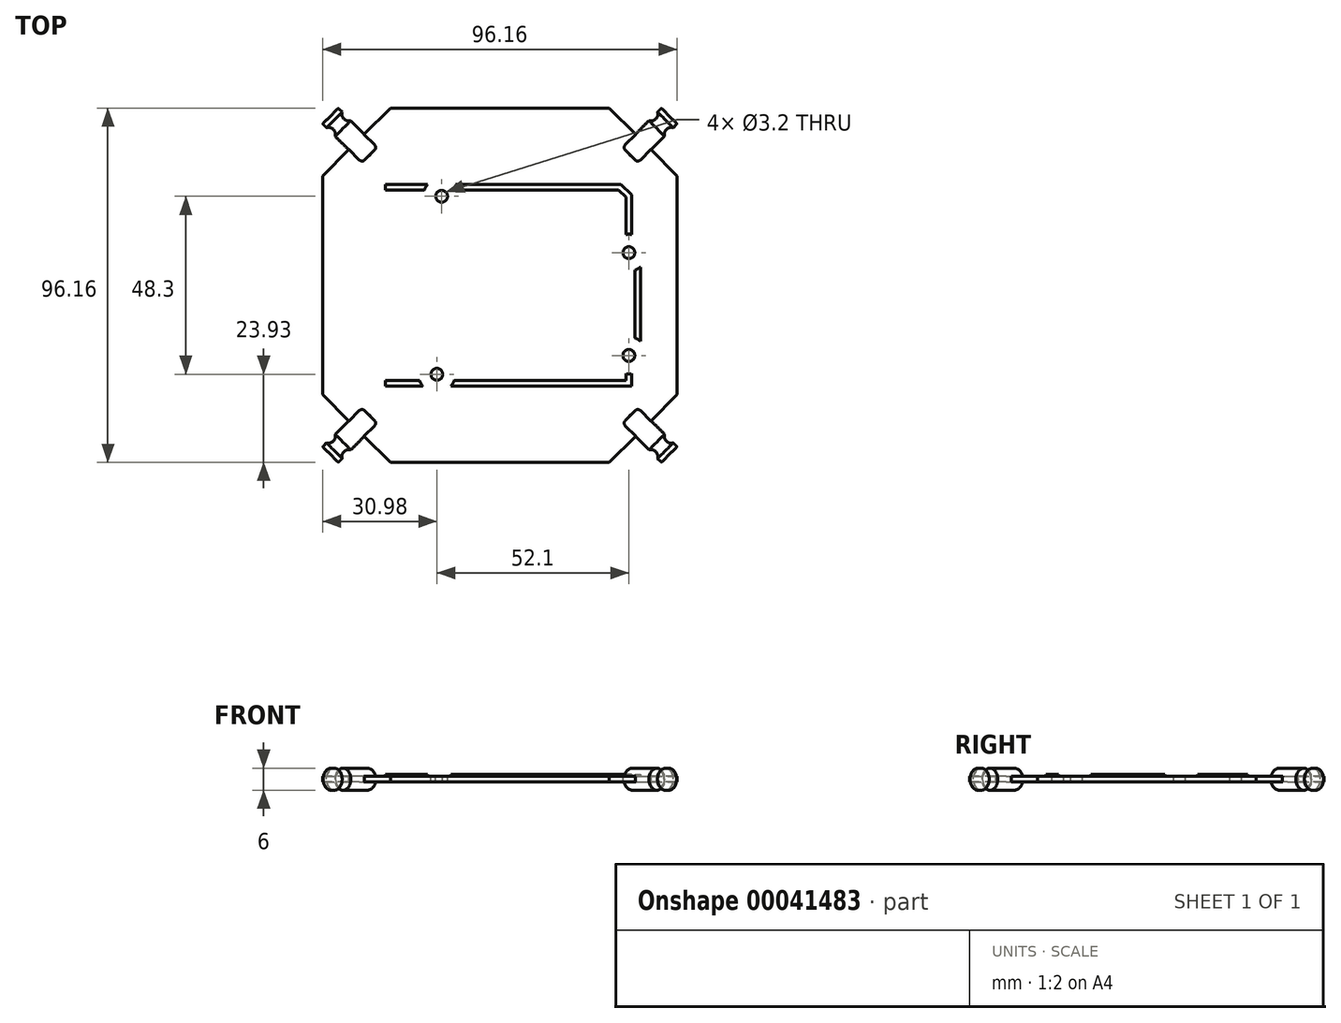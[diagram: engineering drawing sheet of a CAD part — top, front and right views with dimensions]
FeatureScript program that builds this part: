
annotation { "Feature Type Name" : "Feature", "Feature Type Description" : "" }
export const myFeature = defineFeature(function(context is Context, id is Id, definition is map)
    precondition{}
    {
        {
            var Q0;
            Q0=qCreatedBy(makeId("Top.planeOp"),FACE);
            var sketch = newSketch(context, id + "F0", { "sketchPlane" : qUnion([Q0])});
            skLineSegment(sketch, "E0", {"start": v(-43.84, 48.08) * mm, "end": v(43.84, 48.08) * mm, "construction": true});
            skLineSegment(sketch, "E1", {"start": v(48.08, 43.84) * mm, "end": v(43.84, 48.08) * mm, "construction": true});
            skLineSegment(sketch, "E2", {"start": v(48.08, 43.84) * mm, "end": v(48.08, -43.84) * mm, "construction": true});
            skLineSegment(sketch, "E3", {"start": v(48.08, -43.84) * mm, "end": v(43.84, -48.08) * mm, "construction": true});
            skLineSegment(sketch, "E4", {"start": v(43.84, -48.08) * mm, "end": v(-43.84, -48.08) * mm, "construction": true});
            skLineSegment(sketch, "E5", {"start": v(-43.84, -48.08) * mm, "end": v(-48.08, -43.84) * mm, "construction": true});
            skLineSegment(sketch, "E6", {"start": v(-48.08, -43.84) * mm, "end": v(-48.08, 43.84) * mm, "construction": true});
            skLineSegment(sketch, "E7", {"start": v(-43.84, 48.08) * mm, "end": v(-48.08, 43.84) * mm, "construction": true});
            skLineSegment(sketch, "E8", {"start": v(0, 48.08) * mm, "end": v(0, -48.08) * mm, "construction": true});
            skLineSegment(sketch, "E9", {"start": v(-48.08, 0) * mm, "end": v(48.08, 0) * mm, "construction": true});
            skSolve(sketch);
        }
        {
            var Q0;
            Q0=sQuery(id+"F0.wireOp",EDGE,"E3");
            cPlane(context, id + "F1", {"entities" : qUnion([Q0]), "cplaneType" : CPlaneType.LINE_ANGLE, "offset" : 150 * mm, "angle" : 90 * degree, "width" : 150 * mm, "height" : 150 * mm});
        }
        {
            var Q0;
            Q0=qCreatedBy(id+"F1.planeOp",FACE);
            var sketch = newSketch(context, id + "F2", { "sketchPlane" : qUnion([Q0])});
            skCircle(sketch, "E10", {"center": v(0, 0) * mm, "radius": 3 * mm});
            skSolve(sketch);
        }
        {
            var Q0;
            Q0 = qSketchRegion(id + "F2", true);
            extrude(context, id + "F3", {"entities" : qUnion([Q0]), "oppositeDirection" : true, "depth" : 15 * mm});
        }
        {
            var Q0;
            Q0=qCreatedBy(makeId("Top.planeOp"),FACE);
            var sketch = newSketch(context, id + "F4", { "sketchPlane" : qUnion([Q0])});
            skLineSegment(sketch, "E11", {"start": v(47.02, -42.78) * mm, "end": v(44.69, -40.45) * mm});
            skArc(sketch, "E12", {"start": v(44.69, -40.45) * mm, "mid": v(45.15, -42.32) * mm, "end": v(47.02, -42.78) * mm});
            skLineSegment(sketch, "E13", {"start": v(37.48, -33.23) * mm, "end": v(48.08, -43.84) * mm, "construction": true});
            skLineSegment(sketch, "E14", {"start": v(35.36, -35.36) * mm, "end": v(45.96, -45.96) * mm, "construction": true});
            skSolve(sketch);
        }
        {
            var Q0;
            Q0 = qSketchRegion(id + "F4", true);
            var Q1;
            Q1=sQuery(id+"F4.wireOp",EDGE,"E14");
            revolve(context, id + "F5", {"operationType" : NewBodyOperationType.REMOVE, "entities" : qUnion([Q0]), "axis" : qUnion([Q1]), "revolveType" : RevolveType.FULL, "oppositeDirection" : true});
        }
        {
            var Q0;
            Q0=makeQuery(id+"F3.opExtrude","CAP_EDGE",EDGE,{"disambiguationData":[OSD([sQuery(id+"F2.wireOp",EDGE,"E10")])],"isStart":true});
            fillet(context, id + "F6", {"entities" : qUnion([Q0]), "radius" : 0.3 * mm, "tangentPropagation" : true, "allowEdgeOverflow" : false});
        }
        {
            var Q0;
            Q0=makeQuery(id+"F3.opExtrude","CAP_EDGE",EDGE,{"disambiguationData":[OSD([sQuery(id+"F2.wireOp",EDGE,"E10")])],"isStart":false});
            fillet(context, id + "F7", {"entities" : qUnion([Q0]), "radius" : 1 * mm, "tangentPropagation" : true, "allowEdgeOverflow" : false});
        }
        {
            var Q0;
            Q0=qCreatedBy(makeId("Front.planeOp"),FACE);
            var sketch = newSketch(context, id + "F8", { "sketchPlane" : qUnion([Q0])});
            skLineSegment(sketch, "E15", {"start": v(0, 12.87) * mm, "end": v(0, -12.87) * mm, "construction": true});
            skSolve(sketch);
        }
        {
            var Q0;
            Q0=makeQuery(id+"F3.opExtrude","SWEPT_BODY",BODY,{"disambiguationData":[OSD([sQuery(id+"F2.wireOp",EDGE,"E10")])]});
            var Q1;
            Q1=sQuery(id+"F8.wireOp",EDGE,"E15");
            circularPattern(context, id + "F9", {"entities" : qUnion([Q0]), "axis" : qUnion([Q1]), "angle" : 90 * degree, "instanceCount" : 4});
        }
        {
            var Q0;
            Q0=qCreatedBy(makeId("Top.planeOp"),FACE);
            var sketch = newSketch(context, id + "F10", { "sketchPlane" : qUnion([Q0])});
            skLineSegment(sketch, "E16", {"start": v(-29.7, 48.08) * mm, "end": v(-48.08, 29.7) * mm});
            skLineSegment(sketch, "E17", {"start": v(-48.08, 29.7) * mm, "end": v(-48.08, -29.7) * mm});
            skLineSegment(sketch, "E18", {"start": v(-48.08, -29.7) * mm, "end": v(-29.7, -48.08) * mm});
            skLineSegment(sketch, "E19", {"start": v(-29.7, -48.08) * mm, "end": v(29.7, -48.08) * mm});
            skLineSegment(sketch, "E20", {"start": v(29.7, -48.08) * mm, "end": v(48.08, -29.7) * mm});
            skLineSegment(sketch, "E21", {"start": v(48.08, -29.7) * mm, "end": v(48.08, 29.7) * mm});
            skLineSegment(sketch, "E22", {"start": v(48.08, 29.7) * mm, "end": v(29.7, 48.08) * mm});
            skLineSegment(sketch, "E23", {"start": v(29.7, 48.08) * mm, "end": v(-29.7, 48.08) * mm});
            skSolve(sketch);
        }
        {
            var Q0;
            Q0=makeQuery(id+"F10.imprint","IMPRINT",FACE,{"disambiguationData":[TD([[makeQuery(id+"F10.imprint","IMPRINT",EDGE,{"derivedFrom":sQuery(id+"F10.wireOp",EDGE,"E16")}),1.0]])]});
            extrude(context, id + "F11", {"entities" : qUnion([Q0]), "operationType" : NewBodyOperationType.ADD, "endBound" : BoundingType.SYMMETRIC, "depth" : 1.5 * mm});
        }
        {
            var Q0;
            Q0=makeQuery(id+"F11.opExtrude","CAP_FACE",FACE,{"disambiguationData":[OSD([sQuery(id+"F10.wireOp",EDGE,"E16"),sQuery(id+"F10.wireOp",EDGE,"E17"),sQuery(id+"F10.wireOp",EDGE,"E18"),sQuery(id+"F10.wireOp",EDGE,"E19"),sQuery(id+"F10.wireOp",EDGE,"E20"),sQuery(id+"F10.wireOp",EDGE,"E21"),sQuery(id+"F10.wireOp",EDGE,"E22"),sQuery(id+"F10.wireOp",EDGE,"E23")])],"isStart":false});
            var sketch = newSketch(context, id + "F12", { "sketchPlane" : qUnion([Q0])});
            skLineSegment(sketch, "E24.bottom", {"start": v(-31.1, 26.65) * mm, "end": v(37.5, 26.65) * mm, "construction": true});
            skLineSegment(sketch, "E24.top", {"start": v(-31.1, -26.65) * mm, "end": v(37.5, -26.65) * mm, "construction": true});
            skLineSegment(sketch, "E24.left", {"start": v(-31.1, 26.65) * mm, "end": v(-31.1, -26.65) * mm, "construction": true});
            skLineSegment(sketch, "E24.right", {"start": v(37.5, 26.65) * mm, "end": v(37.5, -26.65) * mm, "construction": true});
            skCircle(sketch, "E25", {"center": v(-17.1, -24.15) * mm, "radius": 1.6 * mm});
            skCircle(sketch, "E26", {"center": v(35, -19.05) * mm, "radius": 1.6 * mm});
            skCircle(sketch, "E27", {"center": v(35, 8.85) * mm, "radius": 1.6 * mm});
            skCircle(sketch, "E28", {"center": v(-15.8, 24.15) * mm, "radius": 1.6 * mm});
            skSolve(sketch);
        }
        {
            var Q0;
            Q0=makeQuery(id+"F12.imprint","IMPRINT",FACE,{"disambiguationData":[TD([[makeQuery(id+"F12.imprint","IMPRINT",EDGE,{"derivedFrom":sQuery(id+"F12.wireOp",EDGE,"E28")}),1.0]])]});
            var Q1;
            Q1=makeQuery(id+"F12.imprint","IMPRINT",FACE,{"disambiguationData":[TD([[makeQuery(id+"F12.imprint","IMPRINT",EDGE,{"derivedFrom":sQuery(id+"F12.wireOp",EDGE,"E27")}),1.0]])]});
            var Q2;
            Q2=makeQuery(id+"F12.imprint","IMPRINT",FACE,{"disambiguationData":[TD([[makeQuery(id+"F12.imprint","IMPRINT",EDGE,{"derivedFrom":sQuery(id+"F12.wireOp",EDGE,"E25")}),1.0]])]});
            var Q3;
            Q3=makeQuery(id+"F12.imprint","IMPRINT",FACE,{"disambiguationData":[TD([[makeQuery(id+"F12.imprint","IMPRINT",EDGE,{"derivedFrom":sQuery(id+"F12.wireOp",EDGE,"E26")}),1.0]])]});
            var Q4;
            Q4=makeQuery(id+"F11.opExtrude","CAP_FACE",FACE,{"disambiguationData":[OSD([sQuery(id+"F10.wireOp",EDGE,"E16"),sQuery(id+"F10.wireOp",EDGE,"E17"),sQuery(id+"F10.wireOp",EDGE,"E18"),sQuery(id+"F10.wireOp",EDGE,"E19"),sQuery(id+"F10.wireOp",EDGE,"E20"),sQuery(id+"F10.wireOp",EDGE,"E21"),sQuery(id+"F10.wireOp",EDGE,"E22"),sQuery(id+"F10.wireOp",EDGE,"E23")])],"isStart":true});
            extrude(context, id + "F13", {"entities" : qUnion([Q0, Q1, Q2, Q3]), "operationType" : NewBodyOperationType.REMOVE, "endBound" : BoundingType.UP_TO_SURFACE, "oppositeDirection" : true, "endBoundEntityFace" : qUnion([Q4]), "depth" : 25 * mm});
        }
        {
            var Q0;
            Q0=makeQuery(id+"F12.imprint","IMPRINT",FACE,{"disambiguationData":[TD([[makeQuery(id+"F12.imprint","IMPRINT",EDGE,{"derivedFrom":sQuery(id+"F12.wireOp",EDGE,"E25")}),-1.0]])]});
            var sketch = newSketch(context, id + "F14", { "sketchPlane" : qUnion([Q0])});
            skLineSegment(sketch, "E29", {"start": v(-31.1, 27.4) * mm, "end": v(32.87, 27.4) * mm});
            skLineSegment(sketch, "E30", {"start": v(32.87, 27.4) * mm, "end": v(35.75, 24.52) * mm});
            skLineSegment(sketch, "E31", {"start": v(35.75, 24.52) * mm, "end": v(35.75, 12.48) * mm});
            skLineSegment(sketch, "E32", {"start": v(35.75, 12.48) * mm, "end": v(38.1, 10.13) * mm});
            skLineSegment(sketch, "E33", {"start": v(38.1, 10.13) * mm, "end": v(38.1, -20.33) * mm});
            skLineSegment(sketch, "E34", {"start": v(38.1, -20.33) * mm, "end": v(35.75, -22.68) * mm});
            skLineSegment(sketch, "E35", {"start": v(35.75, -22.68) * mm, "end": v(35.75, -27.4) * mm});
            skLineSegment(sketch, "E36", {"start": v(35.75, -27.4) * mm, "end": v(-31.1, -27.4) * mm});
            skLineSegment(sketch, "E37", {"start": v(-31.1, -27.4) * mm, "end": v(-31.1, -25.9) * mm});
            skLineSegment(sketch, "E38", {"start": v(-31.1, -25.9) * mm, "end": v(34.25, -25.9) * mm});
            skLineSegment(sketch, "E39", {"start": v(34.25, -25.9) * mm, "end": v(34.25, -22.06) * mm});
            skLineSegment(sketch, "E40", {"start": v(34.25, -22.06) * mm, "end": v(36.6, -19.71) * mm});
            skLineSegment(sketch, "E41", {"start": v(36.6, -19.71) * mm, "end": v(36.6, 9.51) * mm});
            skLineSegment(sketch, "E42", {"start": v(36.6, 9.51) * mm, "end": v(34.25, 11.86) * mm});
            skLineSegment(sketch, "E43", {"start": v(34.25, 11.86) * mm, "end": v(34.25, 23.9) * mm});
            skLineSegment(sketch, "E44", {"start": v(34.25, 23.9) * mm, "end": v(32.25, 25.9) * mm});
            skLineSegment(sketch, "E45", {"start": v(32.25, 25.9) * mm, "end": v(-31.1, 25.9) * mm});
            skLineSegment(sketch, "E46", {"start": v(-31.1, 25.9) * mm, "end": v(-31.1, 27.4) * mm});
            skSolve(sketch);
        }
        {
            var Q0;
            Q0 = qSketchRegion(id + "F14", true);
            extrude(context, id + "F15", {"entities" : qUnion([Q0]), "operationType" : NewBodyOperationType.ADD, "depth" : 0.5 * mm});
        }
        {
            var Q0;
            Q0=makeQuery(id+"F12.imprint","IMPRINT",FACE,{"disambiguationData":[TD([[makeQuery(id+"F12.imprint","IMPRINT",EDGE,{"derivedFrom":sQuery(id+"F12.wireOp",EDGE,"E25")}),-1.0]])]});
            var sketch = newSketch(context, id + "F16", { "sketchPlane" : qUnion([Q0])});
            skCircle(sketch, "E47", {"center": v(-15.8, 24.15) * mm, "radius": 5 * mm});
            skCircle(sketch, "E48", {"center": v(35, 8.85) * mm, "radius": 5 * mm});
            skCircle(sketch, "E49", {"center": v(35, -19.05) * mm, "radius": 5 * mm});
            skCircle(sketch, "E50", {"center": v(-17.1, -24.15) * mm, "radius": 5 * mm});
            skSolve(sketch);
        }
        {
            var Q0;
            Q0 = qSketchRegion(id + "F16", true);
            var Q1;
            Q1=makeQuery(id+"F15.opExtrude","CAP_FACE",FACE,{"disambiguationData":[OSD([sQuery(id+"F14.wireOp",EDGE,"E29"),sQuery(id+"F14.wireOp",EDGE,"E30"),sQuery(id+"F14.wireOp",EDGE,"E31"),sQuery(id+"F14.wireOp",EDGE,"E32"),sQuery(id+"F14.wireOp",EDGE,"E33"),sQuery(id+"F14.wireOp",EDGE,"E34"),sQuery(id+"F14.wireOp",EDGE,"E35"),sQuery(id+"F14.wireOp",EDGE,"E36"),sQuery(id+"F14.wireOp",EDGE,"E37"),sQuery(id+"F14.wireOp",EDGE,"E38"),sQuery(id+"F14.wireOp",EDGE,"E39"),sQuery(id+"F14.wireOp",EDGE,"E40"),sQuery(id+"F14.wireOp",EDGE,"E41"),sQuery(id+"F14.wireOp",EDGE,"E42"),sQuery(id+"F14.wireOp",EDGE,"E43"),sQuery(id+"F14.wireOp",EDGE,"E44"),sQuery(id+"F14.wireOp",EDGE,"E45"),sQuery(id+"F14.wireOp",EDGE,"E46")])],"isStart":false});
            extrude(context, id + "F17", {"entities" : qUnion([Q0]), "operationType" : NewBodyOperationType.REMOVE, "endBound" : BoundingType.UP_TO_SURFACE, "endBoundEntityFace" : qUnion([Q1]), "depth" : 25 * mm});
        }
    });
